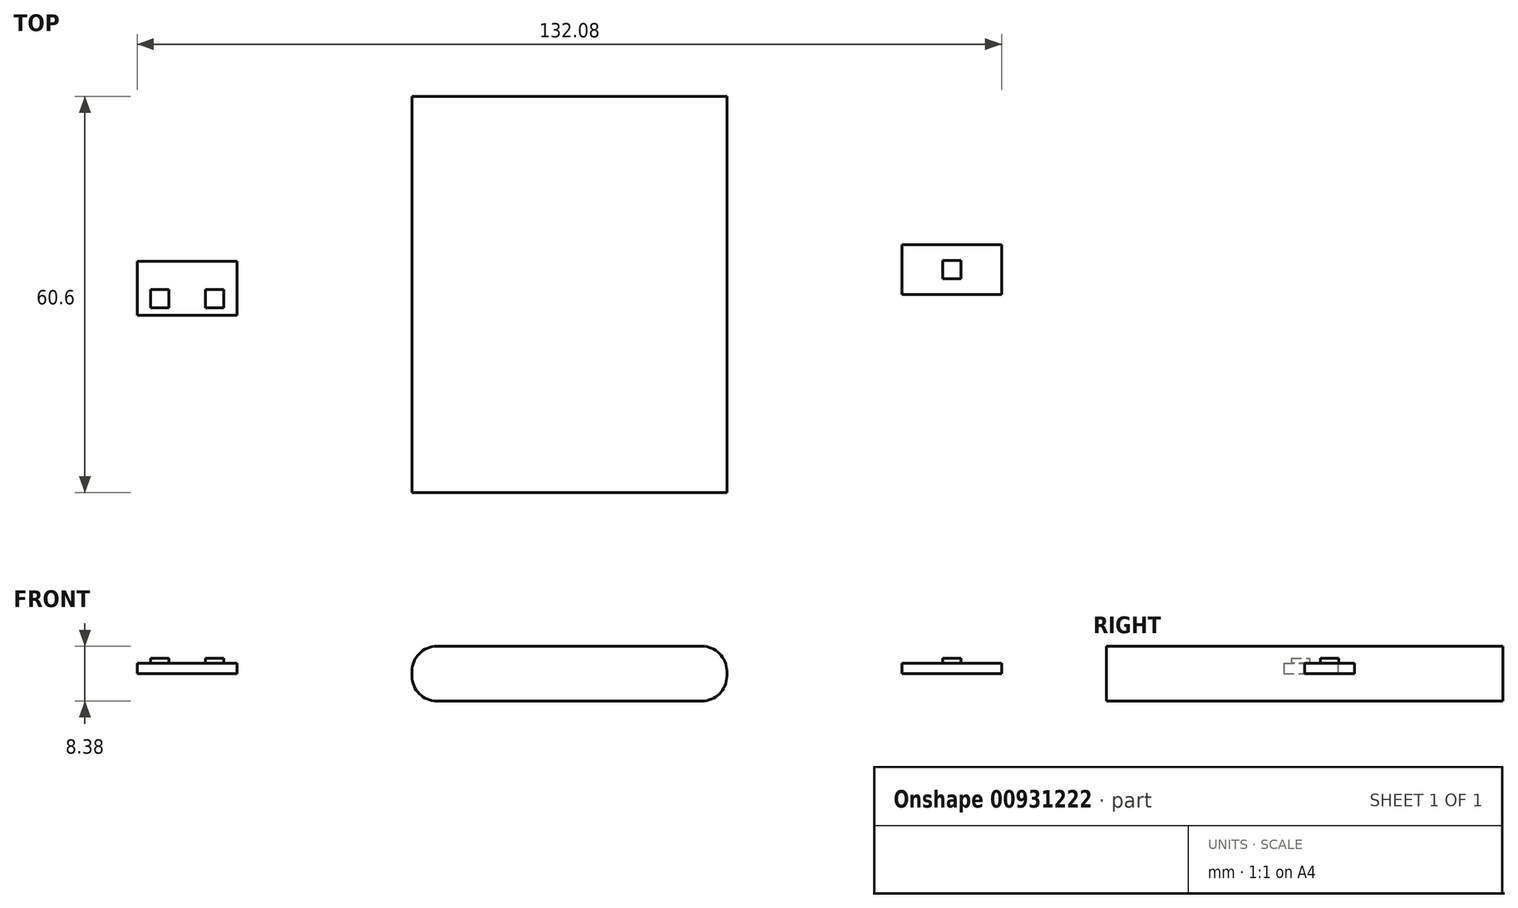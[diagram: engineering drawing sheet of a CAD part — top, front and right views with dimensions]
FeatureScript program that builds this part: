
annotation { "Feature Type Name" : "Feature", "Feature Type Description" : "" }
export const myFeature = defineFeature(function(context is Context, id is Id, definition is map)
    precondition{}
    {
        {
            var Q0;
            Q0=qCreatedBy(makeId("Top.planeOp"),FACE);
            var sketch = newSketch(context, id + "F0", { "sketchPlane" : qUnion([Q0])});
            skLineSegment(sketch, "E0", {"start": v(0, 0) * mm, "end": v(0, 30.3) * mm});
            skLineSegment(sketch, "E1", {"start": v(0, 0) * mm, "end": v(0, -30.3) * mm});
            skLineSegment(sketch, "E2", {"start": v(0, -30.3) * mm, "end": v(-24.05, -30.3) * mm});
            skLineSegment(sketch, "E3", {"start": v(-24.05, -30.3) * mm, "end": v(-24.05, 30.3) * mm});
            skLineSegment(sketch, "E4", {"start": v(-24.05, 30.3) * mm, "end": v(24.05, 30.3) * mm});
            skLineSegment(sketch, "E5", {"start": v(24.05, 30.3) * mm, "end": v(24.05, -30.3) * mm});
            skLineSegment(sketch, "E6", {"start": v(24.05, -30.3) * mm, "end": v(0, -30.3) * mm});
            skSolve(sketch);
        }
        {
            var Q0;
            {var subQ1=sQuery(id+"F0.wireOp",EDGE,"E0");Q0=makeQuery(id+"F0.imprint","IMPRINT",FACE,{"disambiguationData":[TD([[makeQuery(id+"F0.imprint","IMPRINT",EDGE,{"derivedFrom":subQ1}),1.0]])]});}
            var Q1;
            {var subQ2=sQuery(id+"F0.wireOp",EDGE,"E0");Q1=makeQuery(id+"F0.imprint","IMPRINT",FACE,{"disambiguationData":[TD([[makeQuery(id+"F0.imprint","IMPRINT",EDGE,{"derivedFrom":subQ2}),-1.0]])]});}
            extrude(context, id + "F1", {"entities" : qUnion([Q0, Q1]), "endBound" : BoundingType.SYMMETRIC, "depth" : 8.38 * mm, "offsetDistance" : 25.4 * mm});
        }
        {
            var Q0;
            Q0=qCreatedBy(makeId("Top.planeOp"),FACE);
            var sketch = newSketch(context, id + "F2", { "sketchPlane" : qUnion([Q0])});
            skLineSegment(sketch, "E7", {"start": v(0, 0) * mm, "end": v(-50.8, 0) * mm});
            skLineSegment(sketch, "E8", {"start": v(-50.8, 0) * mm, "end": v(-50.8, 5.08) * mm});
            skLineSegment(sketch, "E9", {"start": v(-66.04, 5.08) * mm, "end": v(-66.04, -3.18) * mm});
            skLineSegment(sketch, "E10", {"start": v(-66.04, -3.18) * mm, "end": v(-50.8, -3.18) * mm});
            skLineSegment(sketch, "E11", {"start": v(-50.8, -3.18) * mm, "end": v(-50.8, 0) * mm});
            skLineSegment(sketch, "E12", {"start": v(-50.8, 0) * mm, "end": v(-62.61, 0) * mm});
            skLineSegment(sketch, "E13", {"start": v(-50.8, 0) * mm, "end": v(-54.23, 0) * mm});
            skLineSegment(sketch, "E14", {"start": v(-62.61, -3.18) * mm, "end": v(-62.61, -0.64) * mm});
            skLineSegment(sketch, "E15", {"start": v(-62.61, -0.64) * mm, "end": v(-54.23, -0.64) * mm});
            skLineSegment(sketch, "E16.bottom", {"start": v(-61.21, -2.03) * mm, "end": v(-64, -2.03) * mm});
            skLineSegment(sketch, "E16.top", {"start": v(-61.21, 0.76) * mm, "end": v(-64, 0.76) * mm});
            skLineSegment(sketch, "E16.left", {"start": v(-61.21, -2.03) * mm, "end": v(-61.21, 0.76) * mm});
            skLineSegment(sketch, "E16.right", {"start": v(-64, -2.03) * mm, "end": v(-64, 0.76) * mm});
            skPoint(sketch, "E16.middle", {"position": v(-62.61, -0.64) * mm});
            skLineSegment(sketch, "E17.bottom", {"start": v(-52.83, -2.03) * mm, "end": v(-55.63, -2.03) * mm});
            skLineSegment(sketch, "E17.top", {"start": v(-52.83, 0.76) * mm, "end": v(-55.63, 0.76) * mm});
            skLineSegment(sketch, "E17.left", {"start": v(-52.83, -2.03) * mm, "end": v(-52.83, 0.76) * mm});
            skLineSegment(sketch, "E17.right", {"start": v(-55.63, -2.03) * mm, "end": v(-55.63, 0.76) * mm});
            skPoint(sketch, "E17.middle", {"position": v(-54.23, -0.64) * mm});
            skLineSegment(sketch, "E18", {"start": v(-66.04, 5.08) * mm, "end": v(-50.8, 5.08) * mm});
            skSolve(sketch);
        }
        {
            var Q0;
            {var subQ10=sQuery(id+"F2.wireOp",EDGE,"E8");Q0=makeQuery(id+"F2.imprint","IMPRINT",FACE,{"disambiguationData":[TD([[makeQuery(id+"F2.imprint","IMPRINT",EDGE,{"derivedFrom":subQ10}),1.0]])]});}
            var Q1;
            {var subQ6=sQuery(id+"F2.wireOp",EDGE,"E11");Q1=makeQuery(id+"F2.imprint","IMPRINT",FACE,{"disambiguationData":[TD([[makeQuery(id+"F2.imprint","IMPRINT",EDGE,{"derivedFrom":subQ6}),1.0]])]});}
            var Q2;
            {var subQ0=sQuery(id+"F2.wireOp",EDGE,"E17.right");var subQ1=sQuery(id+"F2.wireOp",EDGE,"E12");var subQ2=makeQuery(id+"F2.imprint","INTERSECT",VERTEX,{"derivedFrom":[subQ1,subQ0]});Q2=makeQuery(id+"F2.imprint","IMPRINT",FACE,{"disambiguationData":[TD([[makeQuery(id+"F2.imprint","IMPRINT",EDGE,{"disambiguationData":[TD([[subQ2,-1.0]])],"derivedFrom":subQ1}),1.0]])]});}
            var Q3;
            {var subQ0=sQuery(id+"F2.wireOp",EDGE,"E16.top");Q3=makeQuery(id+"F2.imprint","IMPRINT",FACE,{"disambiguationData":[TD([[makeQuery(id+"F2.imprint","IMPRINT",EDGE,{"derivedFrom":subQ0}),1.0]])]});}
            var Q4;
            {var subQ0=sQuery(id+"F2.wireOp",EDGE,"E17.bottom");Q4=makeQuery(id+"F2.imprint","IMPRINT",FACE,{"disambiguationData":[TD([[makeQuery(id+"F2.imprint","IMPRINT",EDGE,{"derivedFrom":subQ0}),-1.0]])]});}
            var Q5;
            {var subQ0=sQuery(id+"F2.wireOp",EDGE,"E16.bottom");var subQ1=sQuery(id+"F2.wireOp",EDGE,"E14");var subQ2=makeQuery(id+"F2.imprint","INTERSECT",VERTEX,{"derivedFrom":[subQ1,subQ0]});Q5=makeQuery(id+"F2.imprint","IMPRINT",FACE,{"disambiguationData":[TD([[makeQuery(id+"F2.imprint","IMPRINT",EDGE,{"disambiguationData":[TD([[subQ2,-1.0]])],"derivedFrom":subQ1}),-1.0]])]});}
            var Q6;
            {var subQ0=sQuery(id+"F2.wireOp",EDGE,"E17.top");Q6=makeQuery(id+"F2.imprint","IMPRINT",FACE,{"disambiguationData":[TD([[makeQuery(id+"F2.imprint","IMPRINT",EDGE,{"derivedFrom":subQ0}),1.0]])]});}
            extrude(context, id + "F3", {"entities" : qUnion([Q0, Q1, Q2, Q3, Q4, Q5, Q6]), "depth" : 1.57 * mm, "offsetDistance" : 25.4 * mm});
        }
        {
            var Q0;
            {var subQ0=sQuery(id+"F2.wireOp",EDGE,"E16.top");Q0=makeQuery(id+"F2.imprint","IMPRINT",FACE,{"disambiguationData":[TD([[makeQuery(id+"F2.imprint","IMPRINT",EDGE,{"derivedFrom":subQ0}),1.0]])]});}
            var Q1;
            {var subQ0=sQuery(id+"F2.wireOp",EDGE,"E16.bottom");var subQ1=sQuery(id+"F2.wireOp",EDGE,"E14");var subQ2=makeQuery(id+"F2.imprint","INTERSECT",VERTEX,{"derivedFrom":[subQ1,subQ0]});Q1=makeQuery(id+"F2.imprint","IMPRINT",FACE,{"disambiguationData":[TD([[makeQuery(id+"F2.imprint","IMPRINT",EDGE,{"disambiguationData":[TD([[subQ2,-1.0]])],"derivedFrom":subQ1}),-1.0]])]});}
            var Q2;
            {var subQ0=sQuery(id+"F2.wireOp",EDGE,"E17.bottom");Q2=makeQuery(id+"F2.imprint","IMPRINT",FACE,{"disambiguationData":[TD([[makeQuery(id+"F2.imprint","IMPRINT",EDGE,{"derivedFrom":subQ0}),-1.0]])]});}
            var Q3;
            {var subQ0=sQuery(id+"F2.wireOp",EDGE,"E17.top");Q3=makeQuery(id+"F2.imprint","IMPRINT",FACE,{"disambiguationData":[TD([[makeQuery(id+"F2.imprint","IMPRINT",EDGE,{"derivedFrom":subQ0}),1.0]])]});}
            extrude(context, id + "F4", {"entities" : qUnion([Q0, Q1, Q2, Q3]), "operationType" : NewBodyOperationType.ADD, "depth" : 2.4 * mm, "offsetDistance" : 25.4 * mm});
        }
        {
            var Q0;
            Q0=qCreatedBy(makeId("Top.planeOp"),FACE);
            var sketch = newSketch(context, id + "F5", { "sketchPlane" : qUnion([Q0])});
            skLineSegment(sketch, "E19", {"start": v(0, 0) * mm, "end": v(50.8, 0) * mm});
            skLineSegment(sketch, "E20", {"start": v(50.8, 0) * mm, "end": v(50.8, 7.62) * mm});
            skLineSegment(sketch, "E21", {"start": v(50.8, 7.62) * mm, "end": v(66.04, 7.62) * mm});
            skLineSegment(sketch, "E22", {"start": v(66.04, 7.62) * mm, "end": v(66.04, 0) * mm});
            skLineSegment(sketch, "E23", {"start": v(66.04, 0) * mm, "end": v(50.8, 0) * mm});
            skLineSegment(sketch, "E24", {"start": v(58.42, 0) * mm, "end": v(58.42, 3.81) * mm});
            skPoint(sketch, "E24.endSnap0", {"position": v(66.04, 3.81) * mm});
            skLineSegment(sketch, "E25.bottom", {"start": v(59.82, 2.41) * mm, "end": v(57.02, 2.41) * mm});
            skLineSegment(sketch, "E25.top", {"start": v(59.82, 5.2) * mm, "end": v(57.02, 5.2) * mm});
            skLineSegment(sketch, "E25.left", {"start": v(59.82, 2.41) * mm, "end": v(59.82, 5.2) * mm});
            skLineSegment(sketch, "E25.right", {"start": v(57.02, 2.41) * mm, "end": v(57.02, 5.2) * mm});
            skPoint(sketch, "E25.middle", {"position": v(58.42, 3.81) * mm});
            skSolve(sketch);
        }
        {
            var Q0;
            {var subQ3=sQuery(id+"F5.wireOp",EDGE,"E20");Q0=makeQuery(id+"F5.imprint","IMPRINT",FACE,{"disambiguationData":[TD([[makeQuery(id+"F5.imprint","IMPRINT",EDGE,{"derivedFrom":subQ3}),-1.0]])]});}
            var Q1;
            Q1=makeQuery(id+"F5.imprint","IMPRINT",FACE,{"disambiguationData":[TD([[makeQuery(id+"F5.imprint","IMPRINT",EDGE,{"derivedFrom":sQuery(id+"F5.wireOp",EDGE,"E25.top")}),1.0]])]});
            extrude(context, id + "F6", {"entities" : qUnion([Q0, Q1]), "depth" : 1.57 * mm, "offsetDistance" : 25.4 * mm});
        }
        {
            var Q0;
            Q0=makeQuery(id+"F5.imprint","IMPRINT",FACE,{"disambiguationData":[TD([[makeQuery(id+"F5.imprint","IMPRINT",EDGE,{"derivedFrom":sQuery(id+"F5.wireOp",EDGE,"E25.top")}),1.0]])]});
            extrude(context, id + "F7", {"entities" : qUnion([Q0]), "operationType" : NewBodyOperationType.ADD, "depth" : 2.4 * mm, "offsetDistance" : 25.4 * mm});
        }
        {
            var Q0;
            Q0=makeQuery(id+"F1.opExtrude","CAP_EDGE",EDGE,{"disambiguationData":[OSD([sQuery(id+"F0.wireOp",EDGE,"E3")])],"isStart":false});
            var Q1;
            Q1=makeQuery(id+"F1.opExtrude","CAP_EDGE",EDGE,{"disambiguationData":[OSD([sQuery(id+"F0.wireOp",EDGE,"E3")])],"isStart":true});
            var Q2;
            Q2=makeQuery(id+"F1.opExtrude","CAP_EDGE",EDGE,{"disambiguationData":[OSD([sQuery(id+"F0.wireOp",EDGE,"E5")])],"isStart":false});
            var Q3;
            Q3=makeQuery(id+"F1.opExtrude","CAP_EDGE",EDGE,{"disambiguationData":[OSD([sQuery(id+"F0.wireOp",EDGE,"E5")])],"isStart":true});
            fillet(context, id + "F8", {"entities" : qUnion([Q0, Q1, Q2, Q3]), "radius" : 3.8 * mm, "tangentPropagation" : true, "allowEdgeOverflow" : false});
        }
    });
